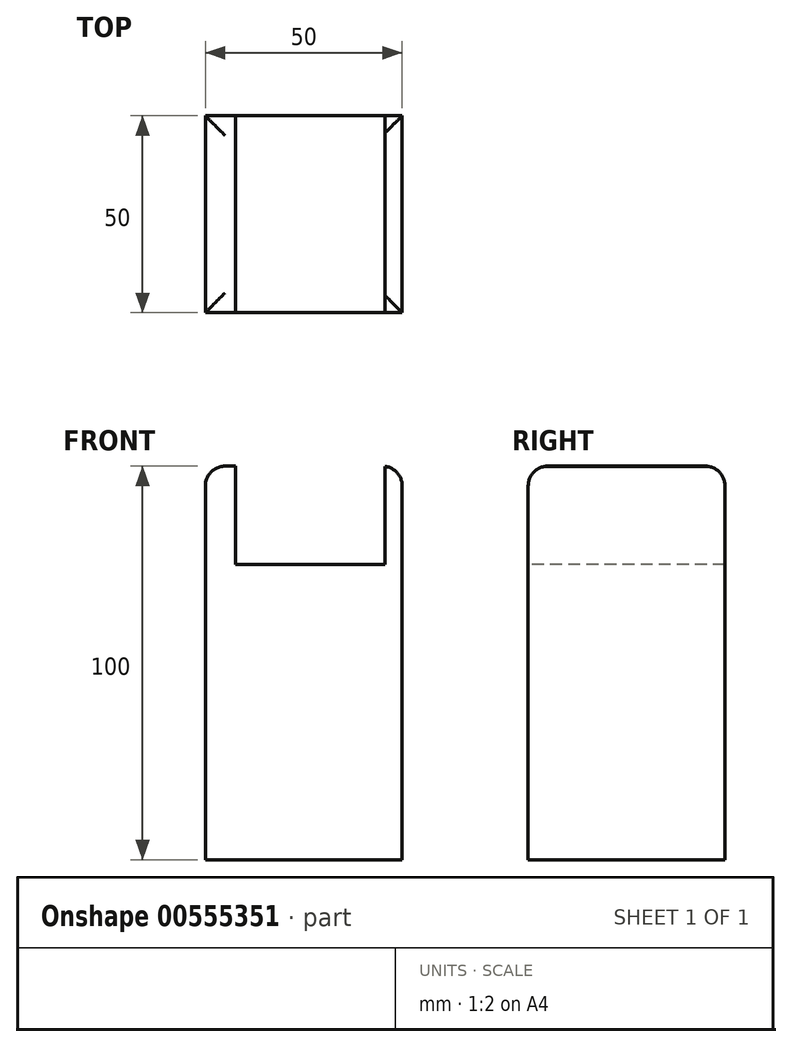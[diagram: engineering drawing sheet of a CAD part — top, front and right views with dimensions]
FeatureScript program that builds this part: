
annotation { "Feature Type Name" : "Feature", "Feature Type Description" : "" }
export const myFeature = defineFeature(function(context is Context, id is Id, definition is map)
    precondition{}
    {
        {
            var Q0;
            Q0=qCreatedBy(makeId("Front.planeOp"),FACE);
            var sketch = newSketch(context, id + "F0", { "sketchPlane" : qUnion([Q0])});
            skLineSegment(sketch, "E0", {"start": v(-68.97, 35.6) * mm, "end": v(-68.97, -64.4) * mm});
            skLineSegment(sketch, "E1", {"start": v(-68.97, -64.4) * mm, "end": v(-18.97, -64.4) * mm});
            skLineSegment(sketch, "E2", {"start": v(-18.97, -64.4) * mm, "end": v(-18.97, 35.6) * mm});
            skLineSegment(sketch, "E3", {"start": v(-18.97, 35.6) * mm, "end": v(-68.97, 35.6) * mm});
            skSolve(sketch);
        }
        {
            var Q0;
            Q0=makeQuery(id+"F0.imprint","IMPRINT",FACE,{"disambiguationData":[TD([[makeQuery(id+"F0.imprint","IMPRINT",EDGE,{"derivedFrom":sQuery(id+"F0.wireOp",EDGE,"E0")}),1.0]])]});
            extrude(context, id + "F1", {"entities" : qUnion([Q0]), "depth" : 50 * mm, "offsetDistance" : 25 * mm});
        }
        {
            var Q0;
            Q0=makeQuery(id+"F1.opExtrude","SWEPT_FACE",FACE,{"disambiguationData":[OSD([sQuery(id+"F0.wireOp",EDGE,"E3")])]});
            fillet(context, id + "F2", {"entities" : qUnion([Q0]), "radius" : 5 * mm, "tangentPropagation" : true, "allowEdgeOverflow" : false});
        }
        {
            var Q0;
            Q0=makeQuery(id+"F1.opExtrude","SWEPT_FACE",FACE,{"disambiguationData":[OSD([sQuery(id+"F0.wireOp",EDGE,"E3")])]});
            var sketch = newSketch(context, id + "F3", { "sketchPlane" : qUnion([Q0])});
            skLineSegment(sketch, "E4", {"start": v(-63.97, -5) * mm, "end": v(-63.97, -45) * mm});
            skLineSegment(sketch, "E5", {"start": v(-63.97, -45) * mm, "end": v(-27.31, -45) * mm});
            skLineSegment(sketch, "E6", {"start": v(-27.31, -45) * mm, "end": v(-27.31, -5) * mm});
            skLineSegment(sketch, "E7", {"start": v(-27.31, -5) * mm, "end": v(-63.97, -5) * mm});
            skSolve(sketch);
        }
        {
            var Q0;
            Q0=makeQuery(id+"F3.imprint","IMPRINT",FACE,{"disambiguationData":[TD([[makeQuery(id+"F3.imprint","IMPRINT",EDGE,{"derivedFrom":sQuery(id+"F3.wireOp",EDGE,"E4")}),1.0]])]});
            var sketch = newSketch(context, id + "F4", { "sketchPlane" : qUnion([Q0])});
            skLineSegment(sketch, "E8", {"start": v(-61.3, 0) * mm, "end": v(-61.3, -53.04) * mm});
            skLineSegment(sketch, "E9", {"start": v(-61.3, -53.04) * mm, "end": v(-23.3, -53.04) * mm});
            skLineSegment(sketch, "E10", {"start": v(-23.3, -53.04) * mm, "end": v(-23.3, 0) * mm});
            skLineSegment(sketch, "E11", {"start": v(-23.3, 0) * mm, "end": v(-61.3, 0) * mm});
            skSolve(sketch);
        }
        {
            var Q0;
            Q0 = qSketchRegion(id + "F4", true);
            extrude(context, id + "F5", {"entities" : qUnion([Q0]), "operationType" : NewBodyOperationType.REMOVE, "oppositeDirection" : true, "depth" : 25 * mm, "offsetDistance" : 25 * mm});
        }
    });
